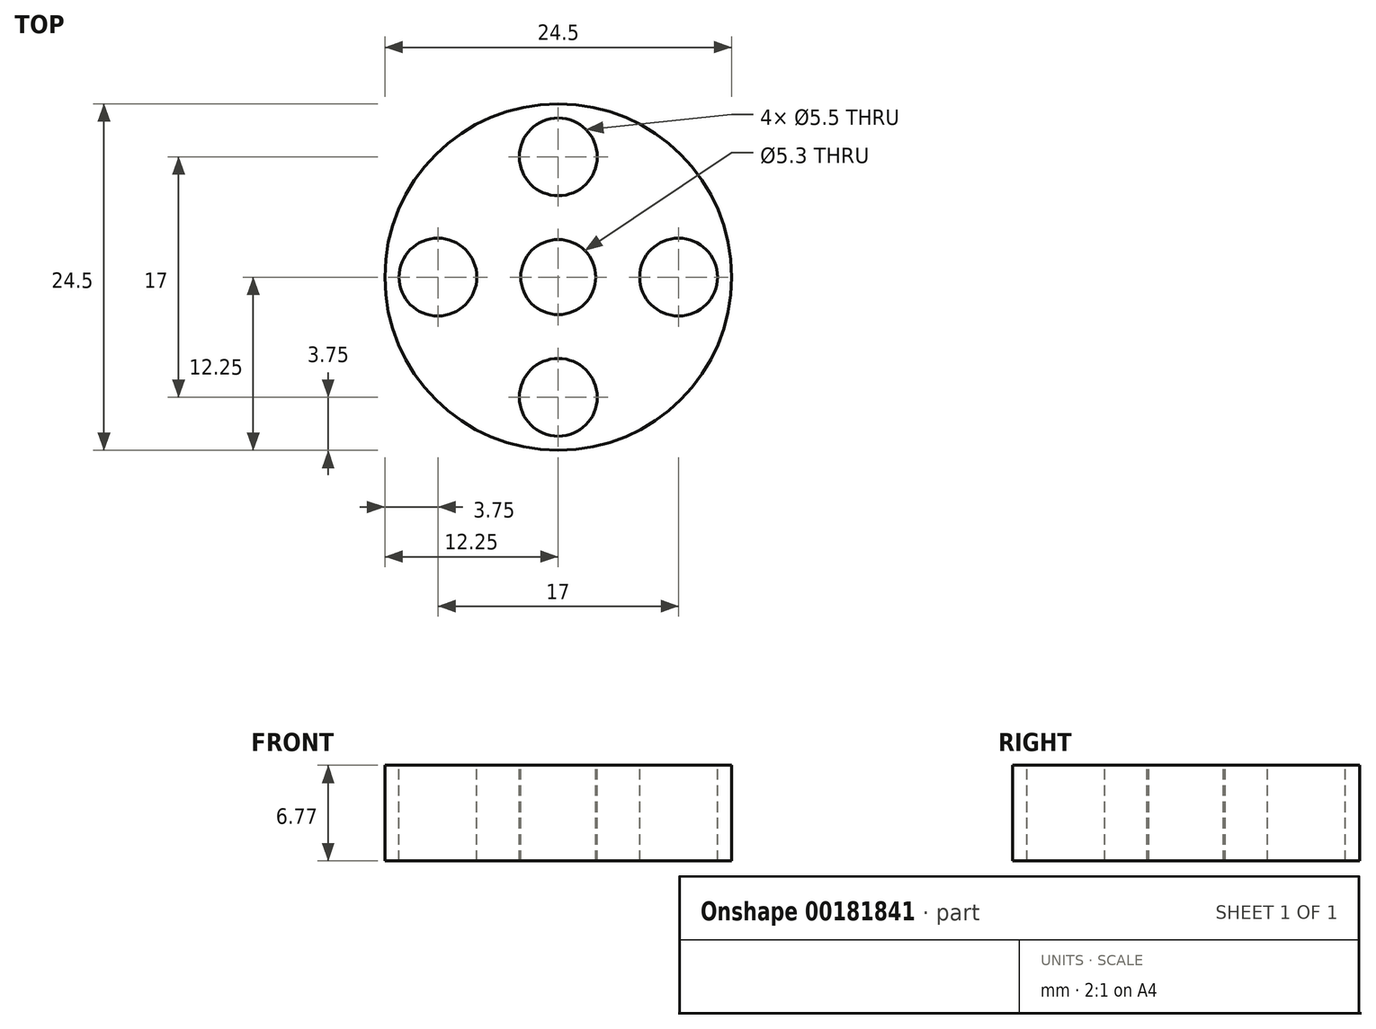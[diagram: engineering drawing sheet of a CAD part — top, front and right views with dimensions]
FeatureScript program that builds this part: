
annotation { "Feature Type Name" : "Feature", "Feature Type Description" : "" }
export const myFeature = defineFeature(function(context is Context, id is Id, definition is map)
    precondition{}
    {
        {
            var Q0;
            Q0=qCreatedBy(makeId("Top.planeOp"),FACE);
            var sketch = newSketch(context, id + "F0", { "sketchPlane" : qUnion([Q0])});
            skCircle(sketch, "E0", {"center": v(0, 0) * mm, "radius": 12.25 * mm});
            skCircle(sketch, "E1", {"center": v(0, 0) * mm, "radius": 8.5 * mm, "construction": true});
            skLineSegment(sketch, "E2", {"start": v(0, 12.25) * mm, "end": v(0, -12.25) * mm, "construction": true});
            skLineSegment(sketch, "E3", {"start": v(12.25, 0) * mm, "end": v(-12.25, 0) * mm, "construction": true});
            skPoint(sketch, "E4", {"position": v(0, 8.5) * mm});
            skPoint(sketch, "E5", {"position": v(-8.5, 0) * mm});
            skPoint(sketch, "E6", {"position": v(0, -8.5) * mm});
            skPoint(sketch, "E7", {"position": v(8.5, 0) * mm});
            skSolve(sketch);
        }
        {
            var Q0;
            Q0=makeQuery(id+"F0.imprint","IMPRINT",FACE,{"disambiguationData":[TD([[makeQuery(id+"F0.imprint","IMPRINT",EDGE,{"derivedFrom":sQuery(id+"F0.wireOp",EDGE,"E0")}),1.0]])]});
            extrude(context, id + "F1", {"entities" : qUnion([Q0]), "oppositeDirection" : true, "depth" : 6.77 * mm});
        }
        {
            var Q0;
            Q0=sQuery(id+"F0.wireOp",VERTEX,"E4");
            var Q1;
            Q1=sQuery(id+"F0.wireOp",VERTEX,"E5");
            var Q2;
            Q2=sQuery(id+"F0.wireOp",VERTEX,"E6");
            var Q3;
            Q3=sQuery(id+"F0.wireOp",VERTEX,"E7");
            var Q4;
            Q4=makeQuery(id+"F1.opExtrude","SWEPT_BODY",BODY,{"disambiguationData":[OSD([sQuery(id+"F0.wireOp",EDGE,"E0")])]});
            hole(context, id + "F2", {"style" : HoleStyle.SIMPLE, "endStyle" : HoleEndStyle.THROUGH, "holeDiameter" : 5.5 * mm, "startFromSketch" : true, "locations" : qUnion([Q0, Q1, Q2, Q3]), "scope" : qUnion([Q4]), "isTappedThrough" : true});
        }
        {
            var Q0;
            Q0=sQuery(id+"F0.wireOp",VERTEX,"E1.center");
            var Q1;
            Q1=makeQuery(id+"F1.opExtrude","SWEPT_BODY",BODY,{"disambiguationData":[OSD([sQuery(id+"F0.wireOp",EDGE,"E0")])]});
            hole(context, id + "F3", {"style" : HoleStyle.SIMPLE, "endStyle" : HoleEndStyle.THROUGH, "holeDiameter" : 5.3 * mm, "startFromSketch" : true, "locations" : qUnion([Q0]), "scope" : qUnion([Q1]), "isTappedThrough" : true});
        }
    });
